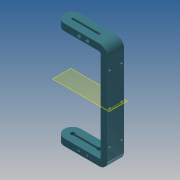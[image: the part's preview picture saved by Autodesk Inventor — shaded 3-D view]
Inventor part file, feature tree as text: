
AUTODESK INVENTOR PART (.ipt)
format: ipt  version: 2013 (Build 170138000, 138)  size: 262,144 bytes
history: native  units: mm
features: extrude x10, sketch x10, pattern_linear x2, projected_geometry x2, fillet x1, plane x1
ambient origin geometry x8: Origin, YZ Plane, XZ Plane, XY Plane, X Axis, Y Axis, Z Axis, Center Point
bodies: Solid1 (feature_tree)
feature tree (26):
  extrude  "Extrusion1"  Depth=25.0mm
  extrude  "Extrusion2"  Depth=160.0mm
  extrude  "Extrusion3"  Depth=10.0mm TaperAngle=0.0deg
  extrude  "Extrusion4"  Depth=5.0mm TaperAngle=0.0deg
  fillet  "Fillet2"  Radius=40.0mm
  extrude  "Extrusion11"  Depth=2.5mm
  extrude  "Extrusion12"  Depth=3.5mm
  extrude  "Extrusion13"  Depth=10.0mm TaperAngle=0.0deg
  extrude  "Extrusion14"  Depth=4.0mm TaperAngle=0.0deg
  pattern_linear  "Rectangular Pattern1"  Spacing1=12.5mm  [1 undecoded]
  extrude  "Extrusion15"  Depth=3.5mm
  extrude  "Extrusion16"  Depth=27.0mm
  plane  "Work Plane1"
  pattern_linear  "Rectangular Pattern2"  Spacing1=10.0mm  [1 undecoded]
  sketch  "Sketch1"  dims[d0=65.0mm d2=25.0mm]
  sketch  "Sketch2"  dims[d3=10.0mm d4=0.0mm d5=160.0mm]
  sketch  "Sketch3"  dims[d6=10.0mm d7=0.0mm d8=10.0mm d9=0.0mm]
  projected_geometry  "Projected Loop1"
  sketch  "Sketch4"  dims[d10=6.0mm d12=5.0mm d13=0.0mm d14=40.0mm]
  sketch  "Sketch11"  dims[d15=150.0mm d16=0.0mm d41=2.5mm d42=12.5mm]
  projected_geometry  "Projected Loop2"
  sketch  "Sketch12"  dims[d49=20.0mm d50=3.5mm]
  sketch  "Sketch13"  dims[d51=18.0mm d52=10.0mm d53=0.0mm]
  sketch  "Sketch14"  dims[d54=5.5mm d55=4.0mm d56=0.0mm]
  sketch  "Sketch15"  dims[d57=3.0mm]
  sketch  "Sketch16"  dims[d59=10.0mm d60=0.0mm d61=12.5mm d63=3.5mm d64=27.0mm d65=10.0mm d66=0.0mm d67=20.0mm d69=150.0mm d70=5.5mm d71=4.0mm d72=0.0mm d73=5.5mm d74=4.0mm d75=0.0mm d76=30.0mm d78=50.0mm]
note: 2 required parameter values undecoded (feature->parameter linkage not recoverable at this tier; creation-order binding heuristic only, values carry confidence <= 0.55)
